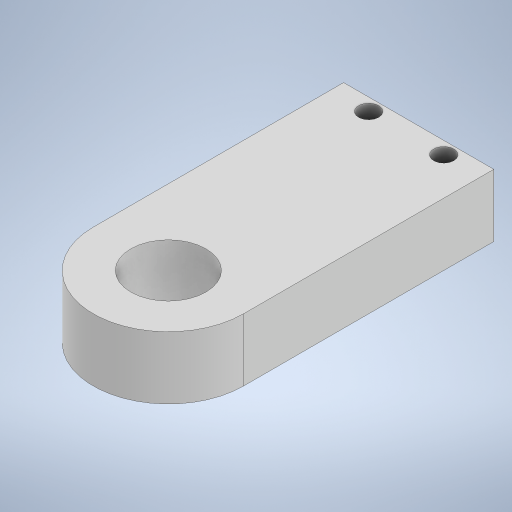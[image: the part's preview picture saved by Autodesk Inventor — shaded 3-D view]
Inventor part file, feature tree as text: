
AUTODESK INVENTOR PART (.ipt)
format: ipt  version: 2023.2 (Build 272271030, 271C)  size: 225,792 bytes
history: native  units: mm
features: extrude x2, sketch x2, projected_geometry x1
ambient origin geometry x8: Origin, YZ Plane, XZ Plane, XY Plane, X Axis, Y Axis, Z Axis, Center Point
bodies: Solid1 (feature_tree)
feature tree (5):
  extrude  "Extrusion1"  Depth=60.0mm
  extrude  "Extrusion2"  Depth=25.0mm TaperAngle=0.0deg
  sketch  "Sketch1"  dims[d0=60.0mm d1=100.0mm]
  sketch  "Sketch2"  dims[d2=30.0mm d3=25.0mm d4=0.0mm d5=10.0mm d6=8.1mm d7=30.0mm d8=0.0mm d9=0.0mm]
  projected_geometry  "Projected Loop1"
